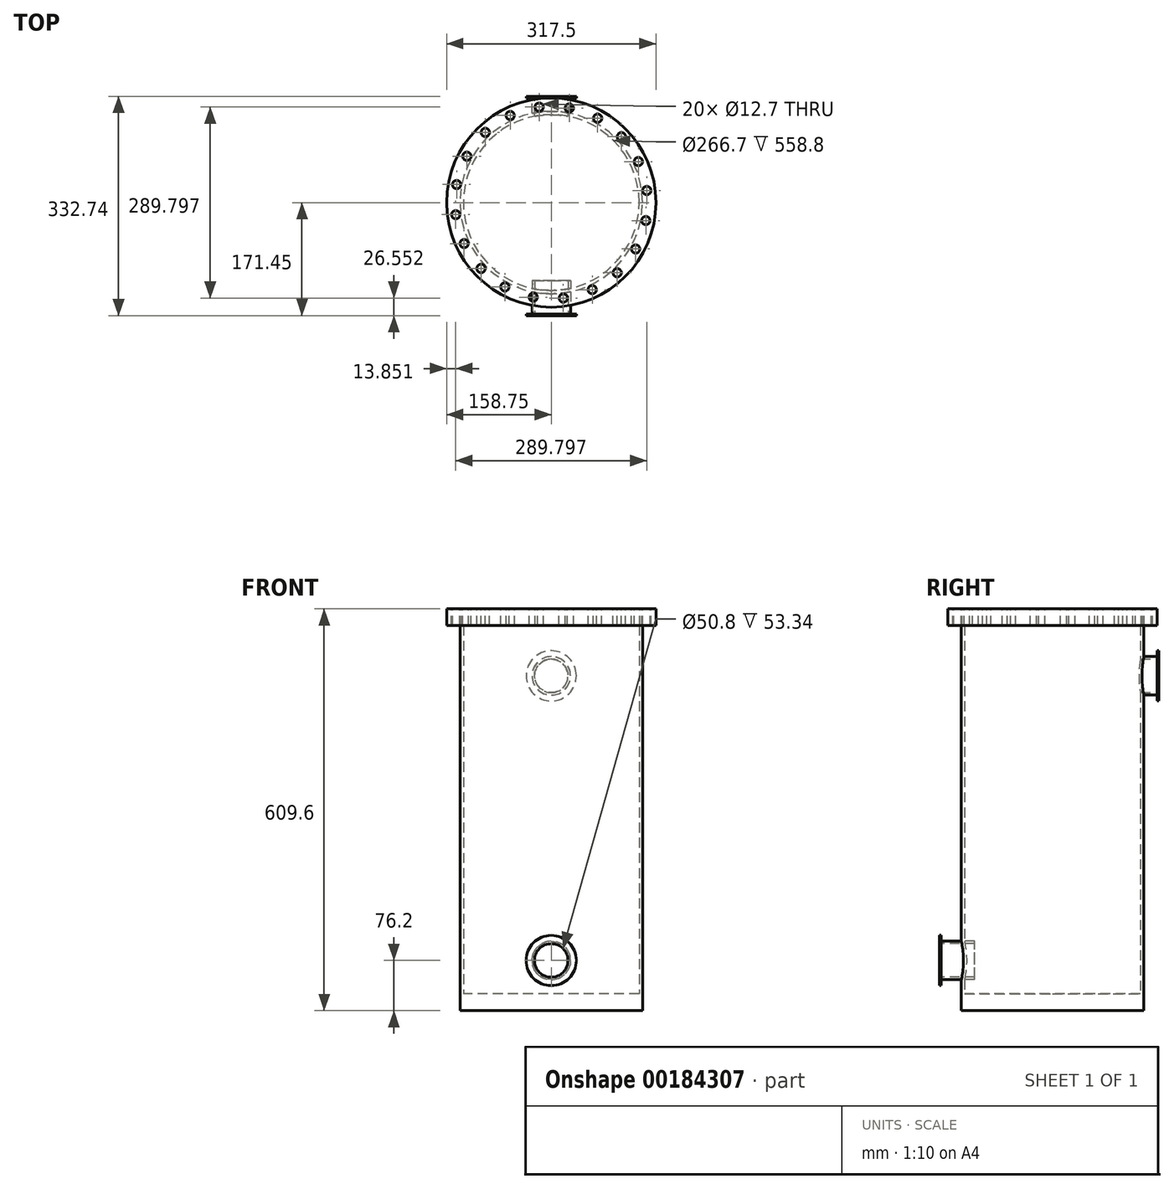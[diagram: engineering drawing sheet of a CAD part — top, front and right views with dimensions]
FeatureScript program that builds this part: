
annotation { "Feature Type Name" : "Feature", "Feature Type Description" : "" }
export const myFeature = defineFeature(function(context is Context, id is Id, definition is map)
    precondition{}
    {
        {
            var Q0;
            Q0=qCreatedBy(makeId("Front.planeOp"),FACE);
            var sketch = newSketch(context, id + "F0", { "sketchPlane" : qUnion([Q0])});
            skCircle(sketch, "E0", {"center": v(0, 0) * mm, "radius": 38.1 * mm});
            skCircle(sketch, "E1", {"center": v(0, 0) * mm, "radius": 29.21 * mm});
            skCircle(sketch, "E2", {"center": v(0, 0) * mm, "radius": 25.4 * mm});
            skSolve(sketch);
        }
        {
            var Q0;
            Q0=makeQuery(id+"F0.imprint","IMPRINT",FACE,{"disambiguationData":[TD([[makeQuery(id+"F0.imprint","IMPRINT",EDGE,{"derivedFrom":sQuery(id+"F0.wireOp",EDGE,"E1")}),1.0]])]});
            extrude(context, id + "F1", {"entities" : qUnion([Q0]), "depth" : 27.94 * mm});
        }
        {
            var Q0;
            Q0=makeQuery(id+"F0.imprint","IMPRINT",FACE,{"disambiguationData":[TD([[makeQuery(id+"F0.imprint","IMPRINT",EDGE,{"derivedFrom":sQuery(id+"F0.wireOp",EDGE,"E0")}),1.0]])]});
            extrude(context, id + "F2", {"entities" : qUnion([Q0]), "operationType" : NewBodyOperationType.ADD, "depth" : 2.54 * mm});
        }
        {
            var Q0;
            Q0=qCreatedBy(makeId("Top.planeOp"),FACE);
            var sketch = newSketch(context, id + "F3", { "sketchPlane" : qUnion([Q0])});
            skLineSegment(sketch, "E3", {"start": v(0, -27.94) * mm, "end": v(0, -161.3) * mm, "construction": true});
            skCircle(sketch, "E4", {"center": v(0, -161.3) * mm, "radius": 133.35 * mm});
            skCircle(sketch, "E5", {"center": v(0, -161.3) * mm, "radius": 138.43 * mm});
            skSolve(sketch);
        }
        {
            var Q0;
            Q0=makeQuery(id+"F3.imprint","IMPRINT",FACE,{"disambiguationData":[TD([[makeQuery(id+"F3.imprint","IMPRINT",EDGE,{"derivedFrom":sQuery(id+"F3.wireOp",EDGE,"E4")}),-1.0]])]});
            extrude(context, id + "F4", {"entities" : qUnion([Q0]), "operationType" : NewBodyOperationType.ADD, "depth" : 76.2 * mm, "hasSecondDirection" : true, "secondDirectionOppositeDirection" : true, "secondDirectionDepth" : 482.6 * mm});
        }
        {
            var Q0;
            Q0=makeQuery(id+"F0.imprint","IMPRINT",FACE,{"disambiguationData":[TD([[makeQuery(id+"F0.imprint","IMPRINT",EDGE,{"derivedFrom":sQuery(id+"F0.wireOp",EDGE,"E2")}),1.0]])]});
            extrude(context, id + "F5", {"entities" : qUnion([Q0]), "operationType" : NewBodyOperationType.REMOVE, "depth" : 47.5 * mm});
        }
        {
            var Q0;
            Q0=makeQuery(id+"F4.opExtrude","CAP_FACE",FACE,{"disambiguationData":[OSD([sQuery(id+"F3.wireOp",EDGE,"E4"),sQuery(id+"F3.wireOp",EDGE,"E5")])],"isStart":false});
            var sketch = newSketch(context, id + "F6", { "sketchPlane" : qUnion([Q0])});
            skCircle(sketch, "E6", {"center": v(0, -161.3) * mm, "radius": 158.75 * mm});
            skSolve(sketch);
        }
        {
            var Q0;
            Q0 = qSketchRegion(id + "F6", true);
            extrude(context, id + "F7", {"entities" : qUnion([Q0]), "operationType" : NewBodyOperationType.ADD, "depth" : 25.4 * mm});
        }
        {
            var Q0;
            Q0=makeQuery(id+"F7.opExtrude","CAP_FACE",FACE,{"disambiguationData":[OSD([sQuery(id+"F6.wireOp",EDGE,"E6")])],"isStart":false});
            var sketch = newSketch(context, id + "F8", { "sketchPlane" : qUnion([Q0])});
            skLineSegment(sketch, "E7", {"start": v(0, -161.3) * mm, "end": v(70.36, -33.3) * mm, "construction": true});
            skCircle(sketch, "E8", {"center": v(70.36, -33.3) * mm, "radius": 6.35 * mm});
            skCircle(sketch, "E9.1.0", {"center": v(27.37, -17.83) * mm, "radius": 6.35 * mm});
            skCircle(sketch, "E9.2.0", {"center": v(-18.3, -16.4) * mm, "radius": 6.35 * mm});
            skCircle(sketch, "E9.3.0", {"center": v(-62.18, -29.14) * mm, "radius": 6.35 * mm});
            skCircle(sketch, "E9.4.0", {"center": v(-99.98, -54.82) * mm, "radius": 6.35 * mm});
            skCircle(sketch, "E9.5.0", {"center": v(-127.98, -90.93) * mm, "radius": 6.35 * mm});
            skCircle(sketch, "E9.6.0", {"center": v(-143.46, -133.92) * mm, "radius": 6.35 * mm});
            skCircle(sketch, "E9.7.0", {"center": v(-144.9, -179.6) * mm, "radius": 6.35 * mm});
            skCircle(sketch, "E9.8.0", {"center": v(-132.15, -223.47) * mm, "radius": 6.35 * mm});
            skCircle(sketch, "E9.9.0", {"center": v(-106.47, -261.27) * mm, "radius": 6.35 * mm});
            skCircle(sketch, "E9.10.0", {"center": v(-70.36, -289.27) * mm, "radius": 6.35 * mm});
            skCircle(sketch, "E9.11.0", {"center": v(-27.37, -304.75) * mm, "radius": 6.35 * mm});
            skCircle(sketch, "E9.12.0", {"center": v(18.3, -306.19) * mm, "radius": 6.35 * mm});
            skCircle(sketch, "E9.13.0", {"center": v(62.18, -293.44) * mm, "radius": 6.35 * mm});
            skCircle(sketch, "E9.14.0", {"center": v(99.98, -267.76) * mm, "radius": 6.35 * mm});
            skCircle(sketch, "E9.15.0", {"center": v(127.98, -231.65) * mm, "radius": 6.35 * mm});
            skCircle(sketch, "E9.16.0", {"center": v(143.46, -188.66) * mm, "radius": 6.35 * mm});
            skCircle(sketch, "E9.17.0", {"center": v(144.9, -142.99) * mm, "radius": 6.35 * mm});
            skCircle(sketch, "E9.18.0", {"center": v(132.15, -99.1) * mm, "radius": 6.35 * mm});
            skCircle(sketch, "E9.19.0", {"center": v(106.47, -61.31) * mm, "radius": 6.35 * mm});
            skPoint(sketch, "E9.center", {"position": v(0, -161.3) * mm});
            skSolve(sketch);
        }
        {
            var Q0;
            Q0=makeQuery(id+"F8.imprint","IMPRINT",FACE,{"disambiguationData":[TD([[makeQuery(id+"F8.imprint","IMPRINT",EDGE,{"derivedFrom":sQuery(id+"F8.wireOp",EDGE,"E9.1.0")}),1.0]])]});
            var Q1;
            Q1=makeQuery(id+"F8.imprint","IMPRINT",FACE,{"disambiguationData":[TD([[makeQuery(id+"F8.imprint","IMPRINT",EDGE,{"derivedFrom":sQuery(id+"F8.wireOp",EDGE,"E8")}),1.0]])]});
            var Q2;
            Q2=makeQuery(id+"F8.imprint","IMPRINT",FACE,{"disambiguationData":[TD([[makeQuery(id+"F8.imprint","IMPRINT",EDGE,{"derivedFrom":sQuery(id+"F8.wireOp",EDGE,"E9.19.0")}),1.0]])]});
            var Q3;
            Q3=makeQuery(id+"F8.imprint","IMPRINT",FACE,{"disambiguationData":[TD([[makeQuery(id+"F8.imprint","IMPRINT",EDGE,{"derivedFrom":sQuery(id+"F8.wireOp",EDGE,"E9.18.0")}),1.0]])]});
            var Q4;
            Q4=makeQuery(id+"F8.imprint","IMPRINT",FACE,{"disambiguationData":[TD([[makeQuery(id+"F8.imprint","IMPRINT",EDGE,{"derivedFrom":sQuery(id+"F8.wireOp",EDGE,"E9.17.0")}),1.0]])]});
            var Q5;
            Q5=makeQuery(id+"F8.imprint","IMPRINT",FACE,{"disambiguationData":[TD([[makeQuery(id+"F8.imprint","IMPRINT",EDGE,{"derivedFrom":sQuery(id+"F8.wireOp",EDGE,"E9.16.0")}),1.0]])]});
            var Q6;
            Q6=makeQuery(id+"F8.imprint","IMPRINT",FACE,{"disambiguationData":[TD([[makeQuery(id+"F8.imprint","IMPRINT",EDGE,{"derivedFrom":sQuery(id+"F8.wireOp",EDGE,"E9.15.0")}),1.0]])]});
            var Q7;
            Q7=makeQuery(id+"F8.imprint","IMPRINT",FACE,{"disambiguationData":[TD([[makeQuery(id+"F8.imprint","IMPRINT",EDGE,{"derivedFrom":sQuery(id+"F8.wireOp",EDGE,"E9.14.0")}),1.0]])]});
            var Q8;
            Q8=makeQuery(id+"F8.imprint","IMPRINT",FACE,{"disambiguationData":[TD([[makeQuery(id+"F8.imprint","IMPRINT",EDGE,{"derivedFrom":sQuery(id+"F8.wireOp",EDGE,"E9.13.0")}),1.0]])]});
            var Q9;
            Q9=makeQuery(id+"F8.imprint","IMPRINT",FACE,{"disambiguationData":[TD([[makeQuery(id+"F8.imprint","IMPRINT",EDGE,{"derivedFrom":sQuery(id+"F8.wireOp",EDGE,"E9.12.0")}),1.0]])]});
            var Q10;
            Q10=makeQuery(id+"F8.imprint","IMPRINT",FACE,{"disambiguationData":[TD([[makeQuery(id+"F8.imprint","IMPRINT",EDGE,{"derivedFrom":sQuery(id+"F8.wireOp",EDGE,"E9.11.0")}),1.0]])]});
            var Q11;
            Q11=makeQuery(id+"F8.imprint","IMPRINT",FACE,{"disambiguationData":[TD([[makeQuery(id+"F8.imprint","IMPRINT",EDGE,{"derivedFrom":sQuery(id+"F8.wireOp",EDGE,"E9.10.0")}),1.0]])]});
            var Q12;
            Q12=makeQuery(id+"F8.imprint","IMPRINT",FACE,{"disambiguationData":[TD([[makeQuery(id+"F8.imprint","IMPRINT",EDGE,{"derivedFrom":sQuery(id+"F8.wireOp",EDGE,"E9.9.0")}),1.0]])]});
            var Q13;
            Q13=makeQuery(id+"F8.imprint","IMPRINT",FACE,{"disambiguationData":[TD([[makeQuery(id+"F8.imprint","IMPRINT",EDGE,{"derivedFrom":sQuery(id+"F8.wireOp",EDGE,"E9.8.0")}),1.0]])]});
            var Q14;
            Q14=makeQuery(id+"F8.imprint","IMPRINT",FACE,{"disambiguationData":[TD([[makeQuery(id+"F8.imprint","IMPRINT",EDGE,{"derivedFrom":sQuery(id+"F8.wireOp",EDGE,"E9.7.0")}),1.0]])]});
            var Q15;
            Q15=makeQuery(id+"F8.imprint","IMPRINT",FACE,{"disambiguationData":[TD([[makeQuery(id+"F8.imprint","IMPRINT",EDGE,{"derivedFrom":sQuery(id+"F8.wireOp",EDGE,"E9.6.0")}),1.0]])]});
            var Q16;
            Q16=makeQuery(id+"F8.imprint","IMPRINT",FACE,{"disambiguationData":[TD([[makeQuery(id+"F8.imprint","IMPRINT",EDGE,{"derivedFrom":sQuery(id+"F8.wireOp",EDGE,"E9.5.0")}),1.0]])]});
            var Q17;
            Q17=makeQuery(id+"F8.imprint","IMPRINT",FACE,{"disambiguationData":[TD([[makeQuery(id+"F8.imprint","IMPRINT",EDGE,{"derivedFrom":sQuery(id+"F8.wireOp",EDGE,"E9.4.0")}),1.0]])]});
            var Q18;
            Q18=makeQuery(id+"F8.imprint","IMPRINT",FACE,{"disambiguationData":[TD([[makeQuery(id+"F8.imprint","IMPRINT",EDGE,{"derivedFrom":sQuery(id+"F8.wireOp",EDGE,"E9.2.0")}),1.0]])]});
            var Q19;
            Q19=makeQuery(id+"F8.imprint","IMPRINT",FACE,{"disambiguationData":[TD([[makeQuery(id+"F8.imprint","IMPRINT",EDGE,{"derivedFrom":sQuery(id+"F8.wireOp",EDGE,"E9.3.0")}),1.0]])]});
            extrude(context, id + "F9", {"entities" : qUnion([Q0, Q1, Q2, Q3, Q4, Q5, Q6, Q7, Q8, Q9, Q10, Q11, Q12, Q13, Q14, Q15, Q16, Q17, Q18, Q19]), "operationType" : NewBodyOperationType.REMOVE, "oppositeDirection" : true, "depth" : 25.4 * mm});
        }
        {
            var Q0;
            Q0=makeQuery(id+"F4.opExtrude","CAP_FACE",FACE,{"disambiguationData":[OSD([sQuery(id+"F3.wireOp",EDGE,"E4"),sQuery(id+"F3.wireOp",EDGE,"E5")])],"isStart":true});
            var sketch = newSketch(context, id + "F10", { "sketchPlane" : qUnion([Q0])});
            skCircle(sketch, "E10", {"center": v(0, 161.3) * mm, "radius": 138.43 * mm});
            skSolve(sketch);
        }
        {
            var Q0;
            Q0 = qSketchRegion(id + "F10", true);
            extrude(context, id + "F11", {"entities" : qUnion([Q0]), "operationType" : NewBodyOperationType.ADD, "depth" : 25.4 * mm});
        }
        {
            var Q0;
            Q0=qCreatedBy(makeId("Front.planeOp"),FACE);
            cPlane(context, id + "F12", {"entities" : qUnion([Q0]), "cplaneType" : CPlaneType.OFFSET, "offset" : 304.8 * mm, "width" : 152.4 * mm, "height" : 152.4 * mm});
        }
        {
            var Q0;
            Q0=qCreatedBy(id+"F12.planeOp",FACE);
            var sketch = newSketch(context, id + "F13", { "sketchPlane" : qUnion([Q0])});
            skLineSegment(sketch, "E11", {"start": v(0, 0) * mm, "end": v(0, -431.8) * mm, "construction": true});
            skCircle(sketch, "E12", {"center": v(0, -431.8) * mm, "radius": 25.4 * mm});
            skCircle(sketch, "E13", {"center": v(0, -431.8) * mm, "radius": 29.21 * mm});
            skSolve(sketch);
        }
        {
            var Q0;
            Q0 = qSketchRegion(id + "F13", true);
            extrude(context, id + "F14", {"entities" : qUnion([Q0]), "operationType" : NewBodyOperationType.ADD, "oppositeDirection" : true, "depth" : 25.4 * mm, "hasSecondDirection" : true, "secondDirectionOppositeDirection" : false, "secondDirectionDepth" : 27.94 * mm});
        }
        {
            var Q0;
            Q0=makeQuery(id+"F14.opExtrude","CAP_FACE",FACE,{"disambiguationData":[OSD([sQuery(id+"F13.wireOp",EDGE,"E12"),sQuery(id+"F13.wireOp",EDGE,"E13")])],"isStart":true});
            var sketch = newSketch(context, id + "F15", { "sketchPlane" : qUnion([Q0])});
            skCircle(sketch, "E14", {"center": v(0, -431.8) * mm, "radius": 38.1 * mm});
            skCircle(sketch, "E15", {"center": v(0, -431.8) * mm, "radius": 29.21 * mm});
            skSolve(sketch);
        }
        {
            var Q0;
            Q0 = qSketchRegion(id + "F15", true);
            extrude(context, id + "F16", {"entities" : qUnion([Q0]), "operationType" : NewBodyOperationType.ADD, "oppositeDirection" : true, "depth" : 2.54 * mm});
        }
        {
            var Q0;
            Q0=makeQuery(id+"F15.imprint","IMPRINT",FACE,{"disambiguationData":[TD([[makeQuery(id+"F15.imprint","IMPRINT",EDGE,{"derivedFrom":makeQuery(id+"F14.opExtrude","CAP_EDGE",EDGE,{"disambiguationData":[OSD([sQuery(id+"F13.wireOp",EDGE,"E12")])],"isStart":true})}),1.0]])]});
            extrude(context, id + "F17", {"entities" : qUnion([Q0]), "operationType" : NewBodyOperationType.REMOVE, "oppositeDirection" : true, "depth" : 50.8 * mm});
        }
    });
